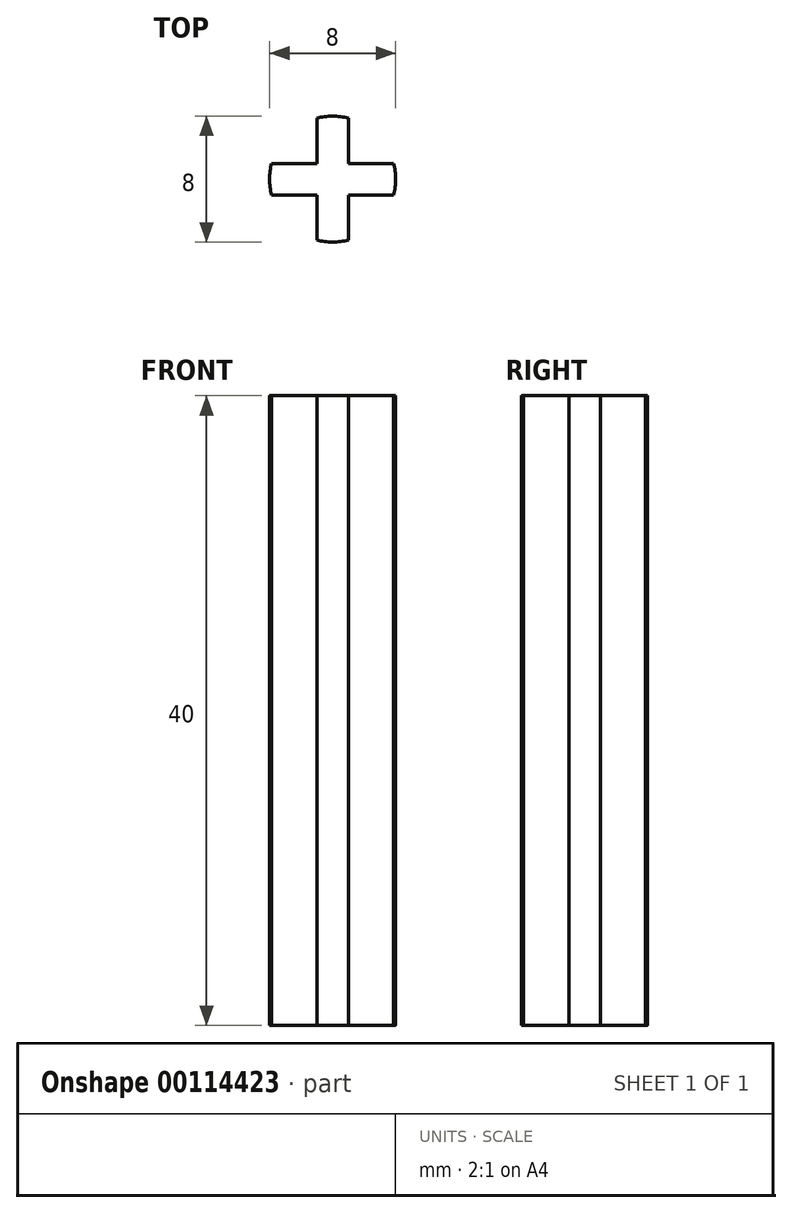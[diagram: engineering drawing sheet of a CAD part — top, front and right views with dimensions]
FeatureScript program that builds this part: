
annotation { "Feature Type Name" : "Feature", "Feature Type Description" : "" }
export const myFeature = defineFeature(function(context is Context, id is Id, definition is map)
    precondition{}
    {
        {
            var Q0;
            Q0=qCreatedBy(makeId("Top.planeOp"),FACE);
            var sketch = newSketch(context, id + "F0", { "sketchPlane" : qUnion([Q0])});
            skCircle(sketch, "E0", {"center": v(0, 0) * mm, "radius": 4 * mm});
            skLineSegment(sketch, "E1.bottom", {"start": v(3.87, -1) * mm, "end": v(-3.87, -1) * mm});
            skLineSegment(sketch, "E1.top", {"start": v(3.87, 1) * mm, "end": v(-3.87, 1) * mm});
            skLineSegment(sketch, "E1.left", {"start": v(3.87, -1) * mm, "end": v(3.87, 1) * mm});
            skLineSegment(sketch, "E1.right", {"start": v(-3.87, -1) * mm, "end": v(-3.87, 1) * mm});
            skLineSegment(sketch, "E2.bottom", {"start": v(1, -3.87) * mm, "end": v(-1, -3.87) * mm});
            skLineSegment(sketch, "E2.top", {"start": v(1, 3.87) * mm, "end": v(-1, 3.87) * mm});
            skLineSegment(sketch, "E2.left", {"start": v(1, -3.87) * mm, "end": v(1, 3.87) * mm});
            skLineSegment(sketch, "E2.right", {"start": v(-1, -3.87) * mm, "end": v(-1, 3.87) * mm});
            skSolve(sketch);
        }
        {
            var Q0;
            {var subQ0=sQuery(id+"F0.wireOp",EDGE,"E2.top");Q0=makeQuery(id+"F0.imprint","IMPRINT",FACE,{"disambiguationData":[TD([[makeQuery(id+"F0.imprint","IMPRINT",EDGE,{"derivedFrom":subQ0}),-1.0]])]});}
            var Q1;
            {var subQ0=sQuery(id+"F0.wireOp",EDGE,"E1.right");Q1=makeQuery(id+"F0.imprint","IMPRINT",FACE,{"disambiguationData":[TD([[makeQuery(id+"F0.imprint","IMPRINT",EDGE,{"derivedFrom":subQ0}),1.0]])]});}
            var Q2;
            {var subQ0=sQuery(id+"F0.wireOp",EDGE,"E2.bottom");Q2=makeQuery(id+"F0.imprint","IMPRINT",FACE,{"disambiguationData":[TD([[makeQuery(id+"F0.imprint","IMPRINT",EDGE,{"derivedFrom":subQ0}),1.0]])]});}
            var Q3;
            {var subQ0=sQuery(id+"F0.wireOp",EDGE,"E1.left");Q3=makeQuery(id+"F0.imprint","IMPRINT",FACE,{"disambiguationData":[TD([[makeQuery(id+"F0.imprint","IMPRINT",EDGE,{"derivedFrom":subQ0}),-1.0]])]});}
            var Q4;
            {var subQ0=sQuery(id+"F0.wireOp",EDGE,"E1.left");Q4=makeQuery(id+"F0.imprint","IMPRINT",FACE,{"disambiguationData":[TD([[makeQuery(id+"F0.imprint","IMPRINT",EDGE,{"derivedFrom":subQ0}),1.0]])]});}
            var Q5;
            {var subQ5=sQuery(id+"F0.wireOp",EDGE,"E2.bottom");Q5=makeQuery(id+"F0.imprint","IMPRINT",FACE,{"disambiguationData":[TD([[makeQuery(id+"F0.imprint","IMPRINT",EDGE,{"derivedFrom":subQ5}),-1.0]])]});}
            var Q6;
            {var subQ0=sQuery(id+"F0.wireOp",EDGE,"E1.right");Q6=makeQuery(id+"F0.imprint","IMPRINT",FACE,{"disambiguationData":[TD([[makeQuery(id+"F0.imprint","IMPRINT",EDGE,{"derivedFrom":subQ0}),-1.0]])]});}
            var Q7;
            {var subQ5=sQuery(id+"F0.wireOp",EDGE,"E2.top");Q7=makeQuery(id+"F0.imprint","IMPRINT",FACE,{"disambiguationData":[TD([[makeQuery(id+"F0.imprint","IMPRINT",EDGE,{"derivedFrom":subQ5}),1.0]])]});}
            var Q8;
            {var subQ0=sQuery(id+"F0.wireOp",EDGE,"E2.left");var subQ1=sQuery(id+"F0.wireOp",EDGE,"E1.bottom");var subQ2=makeQuery(id+"F0.imprint","INTERSECT",VERTEX,{"derivedFrom":[subQ1,subQ0]});Q8=makeQuery(id+"F0.imprint","IMPRINT",FACE,{"disambiguationData":[TD([[makeQuery(id+"F0.imprint","IMPRINT",EDGE,{"disambiguationData":[TD([[subQ2,-1.0]])],"derivedFrom":subQ1}),-1.0]])]});}
            extrude(context, id + "F1", {"entities" : qUnion([Q0, Q1, Q2, Q3, Q4, Q5, Q6, Q7, Q8]), "depth" : 40 * mm});
        }
    });
